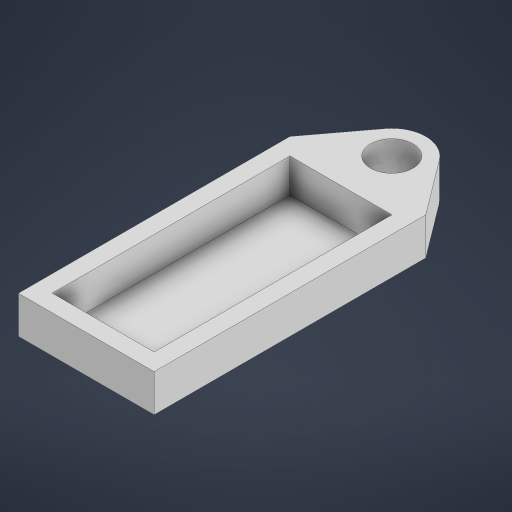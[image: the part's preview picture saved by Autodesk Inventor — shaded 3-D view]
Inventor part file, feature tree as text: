
AUTODESK INVENTOR PART (.ipt)
format: ipt  version: 2024.3 (Build 283343010, 343A)  size: 187,392 bytes
history: native  units: mm
features: extrude x2, sketch x1
ambient origin geometry x8: Origin, YZ Plane, XZ Plane, XY Plane, X Axis, Y Axis, Z Axis, Center Point
bodies: Volumenkörper1 (feature_tree)
feature tree (3):
  sketch  "Skizze1"  dims[d0=12.5mm d1=30.0mm d2=70.0mm d3=15.0mm d4=5.0mm d5=5.0mm d6=5.0mm d7=10.0mm d8=10.0mm d9=0.0mm d10=1.0mm d11=0.0mm]
  extrude  "Extrusion1"  Depth=30.0mm
  extrude  "Extrusion2"  Depth=70.0mm
